# Revit family: ME431
name_source: partatom
category: Communication Devices
units: mm (PartAtom-declared; Revit-internal decimal feet)

## family parameters
Always vertical = Yes
Cut with Voids When Loaded = No
Maintain Annotation Orientation = No
Part Type = Normal
Room Calculation Point = No
Round Connector Dimension = Use Diameter
Shared = No
Work Plane-Based = No

## types (1)
- ME431
    CONNECTIVITY- Input Terminals- Digital = HDMI 2.0 x2, DP 1.2 x1
    CONNECTIVITY- Input Terminals- External Control = LAN (100Mbit), 3.5mm Mini Jack IR Remote, RS-232C
    Default Elevation = 0"
    ENVIRONMENTAL CONDITIONS- Operating Humidity = 20-80%
    ENVIRONMENTAL CONDITIONS- Operating Temperature = 0 to 40C
    LCD MODULE- Aspect Ratio = 16:9
    LCD MODULE- Brightness (Max) = 400 cd/m2
    LCD MODULE- Contrast Ratio (typical) = ≥8000:1
    LCD MODULE- Displayable Colors = Over 1.07 Billion (8 bit + FRC)
    LCD MODULE- Panel Resolution = 3840x2160
    LCD MODULE- Panel Technology = IPS
    LCD MODULE- Viewing Angle (typical) = 178° Vert., 178° Hor. (89U/89D/89L/89R) @ CR>10
    Manufacturer = NEC Display Solutions
    Model = ME431
    PHYSICAL SPECS- Dimensions (W x H x D) = 38.3" x 22.1" x 2.5"
    PHYSICAL SPECS- Weight (Net) = 30.6 lbs
    POWER CONSUMPTION- Max = 175W
    POWER CONSUMPTION- On (typical) = 80W
    URL = www.necdisplay.com

## geometry (parser evidence)
native form markers: Sweep x2
no freeform markers — native parametric forms only
